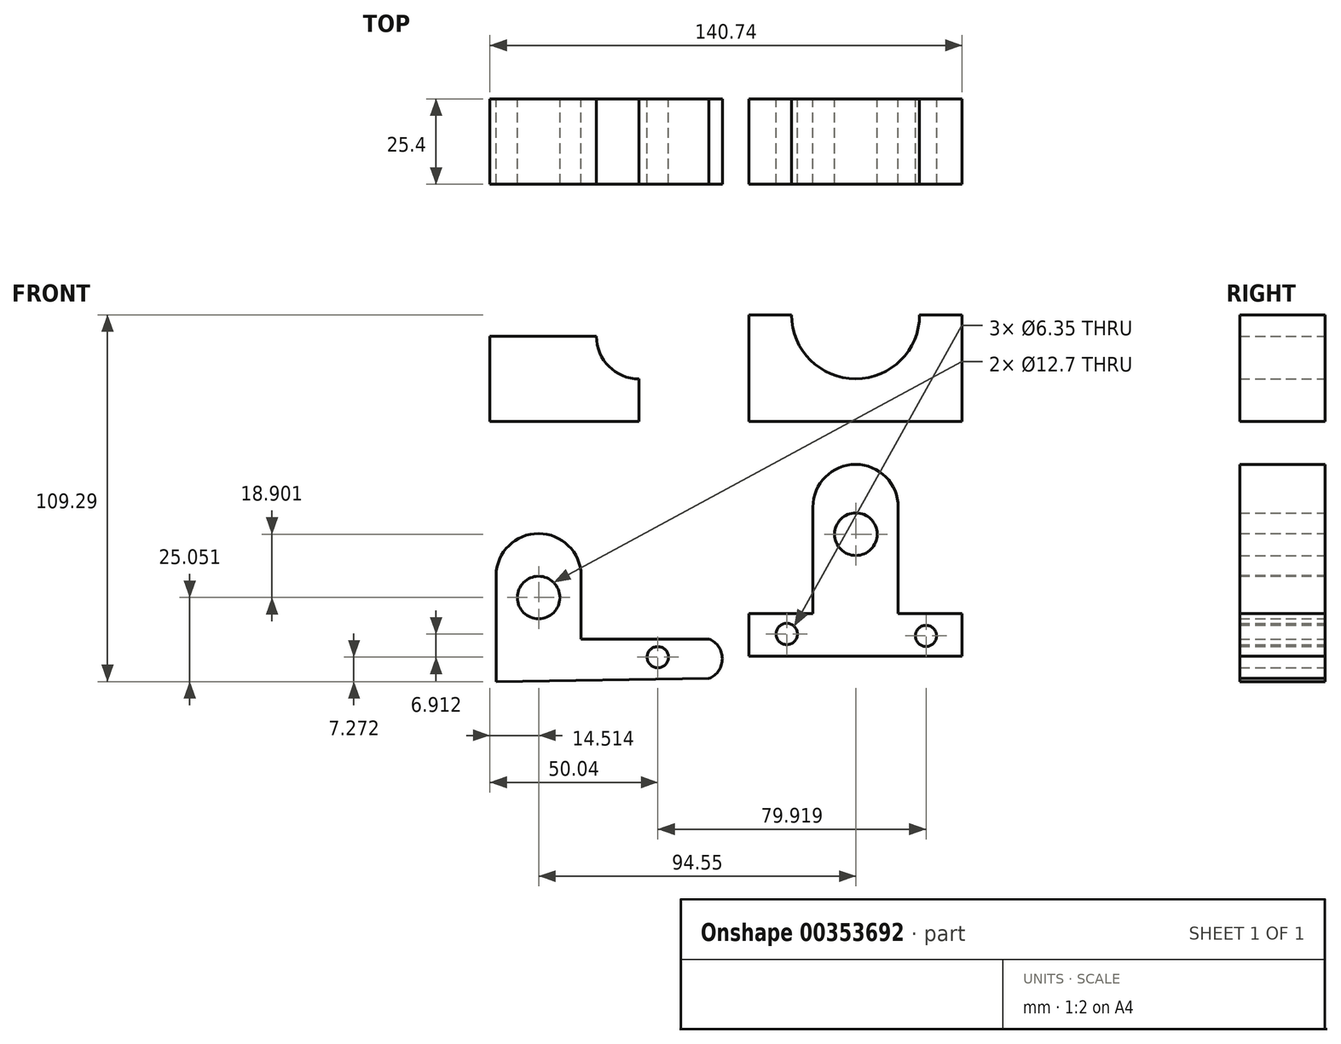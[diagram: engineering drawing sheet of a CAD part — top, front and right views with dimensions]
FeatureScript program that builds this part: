
annotation { "Feature Type Name" : "Feature", "Feature Type Description" : "" }
export const myFeature = defineFeature(function(context is Context, id is Id, definition is map)
    precondition{}
    {
        {
            var Q0;
            Q0=qCreatedBy(makeId("Front.planeOp"),FACE);
            var sketch = newSketch(context, id + "F0", { "sketchPlane" : qUnion([Q0])});
            skLineSegment(sketch, "E0", {"start": v(0, 31.75) * mm, "end": v(0, 0) * mm});
            skLineSegment(sketch, "E1", {"start": v(0, 31.75) * mm, "end": v(12.7, 31.75) * mm});
            skLineSegment(sketch, "E2", {"start": v(0, 0) * mm, "end": v(63.5, 0) * mm});
            skLineSegment(sketch, "E3", {"start": v(63.5, 0) * mm, "end": v(63.5, 31.75) * mm});
            skLineSegment(sketch, "E4", {"start": v(63.5, 31.75) * mm, "end": v(50.8, 31.75) * mm});
            skArc(sketch, "E5", {"start": v(12.7, 31.75) * mm, "mid": v(31.75, 12.7) * mm, "end": v(50.8, 31.75) * mm});
            skLineSegment(sketch, "E6", {"start": v(31.75, 12.7) * mm, "end": v(31.75, 0) * mm});
            skSolve(sketch);
        }
        {
            var Q0;
            Q0 = qSketchRegion(id + "F0", true);
            extrude(context, id + "F1", {"entities" : qUnion([Q0]), "depth" : 25.4 * mm});
        }
        {
            var Q0;
            Q0 = qSketchRegion(id + "F0", true);
            extrude(context, id + "F2", {"entities" : qUnion([Q0]), "operationType" : NewBodyOperationType.ADD, "depth" : 25.4 * mm});
        }
        {
            var Q0;
            Q0=qCreatedBy(makeId("Front.planeOp"),FACE);
            var sketch = newSketch(context, id + "F3", { "sketchPlane" : qUnion([Q0])});
            skLineSegment(sketch, "E7", {"start": v(-77.24, 0) * mm, "end": v(-77.24, 25.4) * mm});
            skLineSegment(sketch, "E8", {"start": v(-77.24, 25.4) * mm, "end": v(-45.49, 25.4) * mm});
            skArc(sketch, "E9", {"start": v(-45.49, 25.4) * mm, "mid": v(-41.77, 16.42) * mm, "end": v(-32.79, 12.7) * mm});
            skLineSegment(sketch, "E10", {"start": v(-32.79, 12.7) * mm, "end": v(-32.79, 0) * mm});
            skLineSegment(sketch, "E11", {"start": v(-77.24, 0) * mm, "end": v(-32.79, 0) * mm});
            skSolve(sketch);
        }
        {
            var Q0;
            Q0 = qSketchRegion(id + "F3", true);
            extrude(context, id + "F4", {"entities" : qUnion([Q0]), "depth" : 25.4 * mm});
        }
        {
            var Q0;
            Q0=qCreatedBy(makeId("Front.planeOp"),FACE);
            var sketch = newSketch(context, id + "F5", { "sketchPlane" : qUnion([Q0])});
            skLineSegment(sketch, "E12", {"start": v(-75.42, -77.54) * mm, "end": v(-75.42, -45.8) * mm});
            skArc(sketch, "E13", {"start": v(-50.03, -45.8) * mm, "mid": v(-62.73, -33.4) * mm, "end": v(-75.42, -45.8) * mm});
            skLineSegment(sketch, "E14", {"start": v(-50.03, -45.8) * mm, "end": v(-50.03, -64.84) * mm});
            skLineSegment(sketch, "E15", {"start": v(-50.03, -64.84) * mm, "end": v(-11.93, -64.84) * mm});
            skArc(sketch, "E16", {"start": v(-11.93, -76.6) * mm, "mid": v(-7.99, -70.72) * mm, "end": v(-11.93, -64.84) * mm});
            skLineSegment(sketch, "E17", {"start": v(-75.42, -77.54) * mm, "end": v(-11.93, -76.6) * mm});
            skCircle(sketch, "E18", {"center": v(-62.73, -52.49) * mm, "radius": 6.35 * mm});
            skArc(sketch, "E19", {"start": v(-28.89, -68.94) * mm, "mid": v(-27.51, -70.24) * mm, "end": v(-25.77, -69.51) * mm});
            skCircle(sketch, "E20", {"center": v(-27.2, -70.27) * mm, "radius": 3.18 * mm});
            skSolve(sketch);
        }
        {
            var Q0;
            Q0 = qSketchRegion(id + "F5", true);
            extrude(context, id + "F6", {"entities" : qUnion([Q0]), "depth" : 25.4 * mm});
        }
        {
            var Q0;
            Q0=qCreatedBy(makeId("Front.planeOp"),FACE);
            var sketch = newSketch(context, id + "F7", { "sketchPlane" : qUnion([Q0])});
            skLineSegment(sketch, "E21", {"start": v(0, -69.94) * mm, "end": v(0, -57.24) * mm});
            skLineSegment(sketch, "E22", {"start": v(0, -57.24) * mm, "end": v(19.05, -57.24) * mm});
            skLineSegment(sketch, "E23", {"start": v(19.05, -57.24) * mm, "end": v(19.05, -25.5) * mm});
            skArc(sketch, "E24", {"start": v(44.45, -25.5) * mm, "mid": v(31.75, -12.8) * mm, "end": v(19.05, -25.5) * mm});
            skLineSegment(sketch, "E25", {"start": v(44.45, -25.5) * mm, "end": v(44.45, -57.24) * mm});
            skLineSegment(sketch, "E26", {"start": v(44.45, -57.24) * mm, "end": v(63.5, -57.24) * mm});
            skLineSegment(sketch, "E27", {"start": v(63.5, -57.24) * mm, "end": v(63.5, -69.94) * mm});
            skLineSegment(sketch, "E28", {"start": v(63.5, -69.94) * mm, "end": v(0, -69.94) * mm});
            skCircle(sketch, "E29", {"center": v(31.82, -33.59) * mm, "radius": 6.35 * mm});
            skCircle(sketch, "E30", {"center": v(11.22, -63.36) * mm, "radius": 3.18 * mm});
            skCircle(sketch, "E31", {"center": v(52.72, -63.93) * mm, "radius": 3.18 * mm});
            skSolve(sketch);
        }
        {
            var Q0;
            Q0 = qSketchRegion(id + "F7", true);
            extrude(context, id + "F8", {"entities" : qUnion([Q0]), "depth" : 25.4 * mm});
        }
        {
            var Q0;
            Q0 = qSketchRegion(id + "F7", true);
            extrude(context, id + "F9", {"entities" : qUnion([Q0]), "operationType" : NewBodyOperationType.ADD, "depth" : 25.4 * mm});
        }
    });
